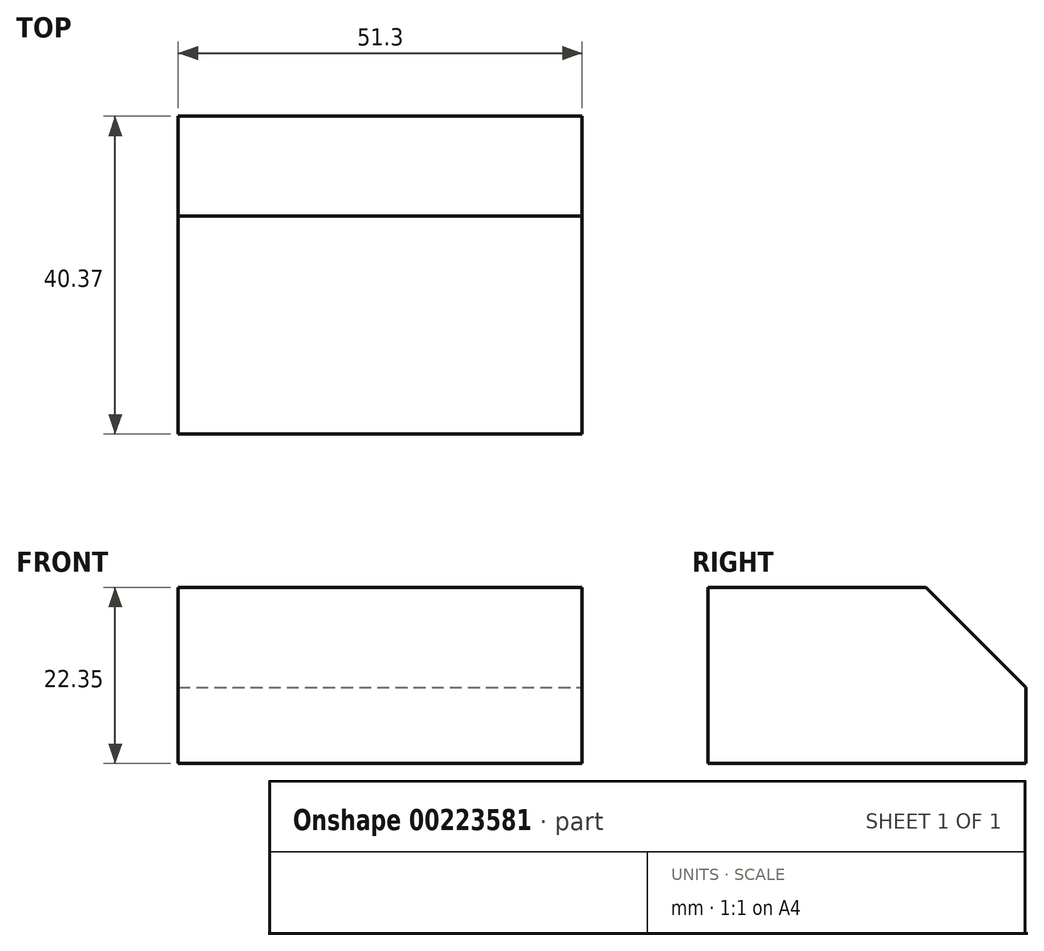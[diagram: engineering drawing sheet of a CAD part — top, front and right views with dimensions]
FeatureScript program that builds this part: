
annotation { "Feature Type Name" : "Feature", "Feature Type Description" : "" }
export const myFeature = defineFeature(function(context is Context, id is Id, definition is map)
    precondition{}
    {
        {
            var Q0;
            Q0=qCreatedBy(makeId("Top.planeOp"),FACE);
            var sketch = newSketch(context, id + "F0", { "sketchPlane" : qUnion([Q0])});
            skLineSegment(sketch, "E0.bottom", {"start": v(0, 0) * mm, "end": v(51.3, 0) * mm});
            skLineSegment(sketch, "E0.top", {"start": v(0, 40.37) * mm, "end": v(51.3, 40.37) * mm});
            skLineSegment(sketch, "E0.left", {"start": v(0, 0) * mm, "end": v(0, 40.37) * mm});
            skLineSegment(sketch, "E0.right", {"start": v(51.3, 0) * mm, "end": v(51.3, 40.37) * mm});
            skSolve(sketch);
        }
        {
            var Q0;
            Q0 = qSketchRegion(id + "F0", true);
            extrude(context, id + "F1", {"entities" : qUnion([Q0]), "depth" : 22.35 * mm});
        }
        {
            var Q0;
            Q0=makeQuery(id+"F1.opExtrude","CAP_EDGE",EDGE,{"disambiguationData":[OSD([sQuery(id+"F0.wireOp",EDGE,"E0.top")])],"isStart":false});
            chamfer(context, id + "F2", {"entities" : qUnion([Q0]), "width" : 12.7 * mm, "tangentPropagation" : true});
        }
    });
